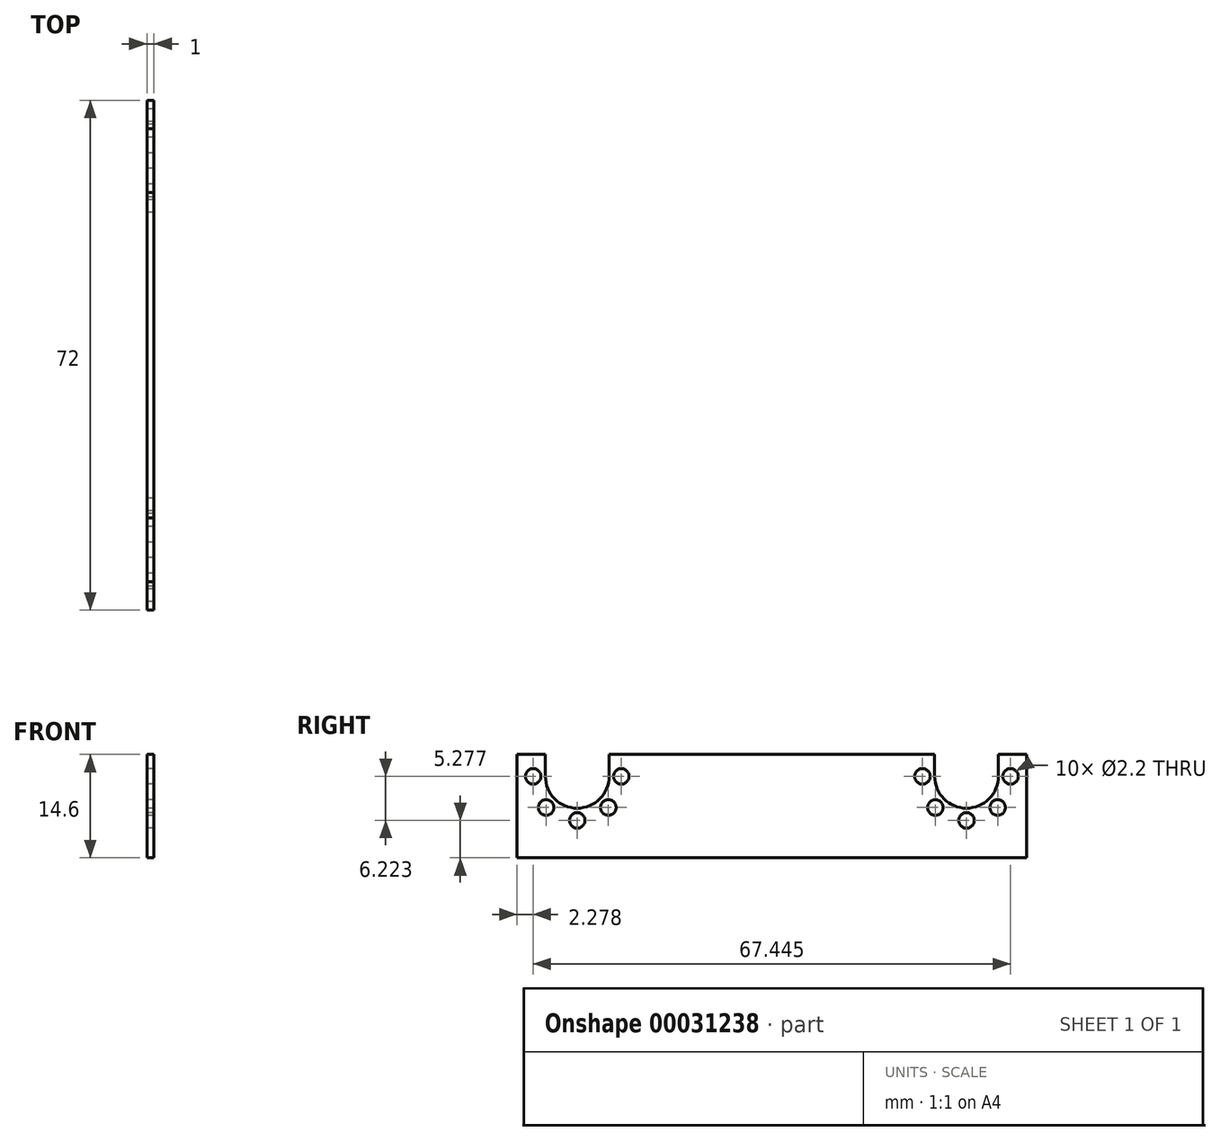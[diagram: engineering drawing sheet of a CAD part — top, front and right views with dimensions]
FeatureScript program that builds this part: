
annotation { "Feature Type Name" : "Feature", "Feature Type Description" : "" }
export const myFeature = defineFeature(function(context is Context, id is Id, definition is map)
    precondition{}
    {
        {
            var Q0;
            Q0=qCreatedBy(makeId("Front.planeOp"),FACE);
            var sketch = newSketch(context, id + "F0", { "sketchPlane" : qUnion([Q0])});
            skLineSegment(sketch, "E0", {"start": v(0, 20) * mm, "end": v(0, 0) * mm});
            skLineSegment(sketch, "E1", {"start": v(-1, 0) * mm, "end": v(-1, 20) * mm});
            skLineSegment(sketch, "E2", {"start": v(-1, 20) * mm, "end": v(0, 20) * mm});
            skLineSegment(sketch, "E3", {"start": v(-1, 0) * mm, "end": v(0, 0) * mm});
            skSolve(sketch);
        }
        {
            var Q0;
            Q0 = qSketchRegion(id + "F0", true);
            extrude(context, id + "F1", {"entities" : qUnion([Q0]), "depth" : 72 * mm});
        }
        {
            var Q0;
            Q0=makeQuery(id+"F1.opExtrude","SWEPT_FACE",FACE,{"disambiguationData":[OSD([sQuery(id+"F0.wireOp",EDGE,"E1")])]});
            var sketch = newSketch(context, id + "F2", { "sketchPlane" : qUnion([Q0])});
            skArc(sketch, "E4", {"start": v(4, 11.5) * mm, "mid": v(8.5, 7) * mm, "end": v(13, 11.5) * mm});
            skCircle(sketch, "E5", {"center": v(2.28, 11.5) * mm, "radius": 1.1 * mm});
            skCircle(sketch, "E6.1.0", {"center": v(4.1, 7.1) * mm, "radius": 1.1 * mm});
            skCircle(sketch, "E6.2.0", {"center": v(8.5, 5.28) * mm, "radius": 1.1 * mm});
            skCircle(sketch, "E6.3.0", {"center": v(12.9, 7.1) * mm, "radius": 1.1 * mm});
            skCircle(sketch, "E7.1.4.0", {"center": v(14.72, 11.5) * mm, "radius": 1.1 * mm});
            skPoint(sketch, "E8", {"position": v(4, 11.5) * mm});
            skPoint(sketch, "E9", {"position": v(13, 11.5) * mm});
            skLineSegment(sketch, "E10", {"start": v(4, 11.5) * mm, "end": v(4, 20) * mm});
            skLineSegment(sketch, "E11", {"start": v(13, 11.5) * mm, "end": v(13, 20) * mm});
            skLineSegment(sketch, "E12", {"start": v(13, 20) * mm, "end": v(4, 20) * mm});
            skLineSegment(sketch, "E13", {"start": v(36, 20) * mm, "end": v(36, 0) * mm, "construction": true});
            skLineSegment(sketch, "E14.MirrorCS", {"start": v(68, 11.5) * mm, "end": v(68, 20) * mm});
            skCircle(sketch, "E15.MirrorC", {"center": v(69.72, 11.5) * mm, "radius": 1.1 * mm});
            skCircle(sketch, "E16.MirrorC", {"center": v(67.9, 7.1) * mm, "radius": 1.1 * mm});
            skCircle(sketch, "E17.MirrorC", {"center": v(63.5, 5.28) * mm, "radius": 1.1 * mm});
            skCircle(sketch, "E18.MirrorC", {"center": v(59.1, 7.1) * mm, "radius": 1.1 * mm});
            skCircle(sketch, "E19.MirrorC", {"center": v(57.28, 11.5) * mm, "radius": 1.1 * mm});
            skLineSegment(sketch, "E20.MirrorCS", {"start": v(59, 11.5) * mm, "end": v(59, 20) * mm});
            skLineSegment(sketch, "E21.MirrorCS", {"start": v(59, 20) * mm, "end": v(68, 20) * mm});
            skArc(sketch, "E22.MirrorCS", {"start": v(68, 11.5) * mm, "mid": v(63.5, 7) * mm, "end": v(59, 11.5) * mm});
            skSolve(sketch);
        }
        {
            var Q0;
            Q0 = qSketchRegion(id + "F2", true);
            extrude(context, id + "F3", {"entities" : qUnion([Q0]), "operationType" : NewBodyOperationType.REMOVE, "endBound" : BoundingType.THROUGH_ALL, "oppositeDirection" : true, "depth" : 25 * mm});
        }
        {
            var Q0;
            Q0=makeQuery(id+"F1.opExtrude","SWEPT_FACE",FACE,{"disambiguationData":[OSD([sQuery(id+"F0.wireOp",EDGE,"E1")])]});
            var sketch = newSketch(context, id + "F4", { "sketchPlane" : qUnion([Q0])});
            skLineSegment(sketch, "E23.bottom", {"start": v(0, 20) * mm, "end": v(72, 20) * mm});
            skLineSegment(sketch, "E23.top", {"start": v(0, 14.6) * mm, "end": v(72, 14.6) * mm});
            skLineSegment(sketch, "E23.left", {"start": v(0, 20) * mm, "end": v(0, 14.6) * mm});
            skLineSegment(sketch, "E23.right", {"start": v(72, 20) * mm, "end": v(72, 14.6) * mm});
            skSolve(sketch);
        }
        {
            var Q0;
            Q0 = qSketchRegion(id + "F4", true);
            extrude(context, id + "F5", {"entities" : qUnion([Q0]), "operationType" : NewBodyOperationType.REMOVE, "endBound" : BoundingType.THROUGH_ALL, "oppositeDirection" : true, "depth" : 25 * mm});
        }
    });
